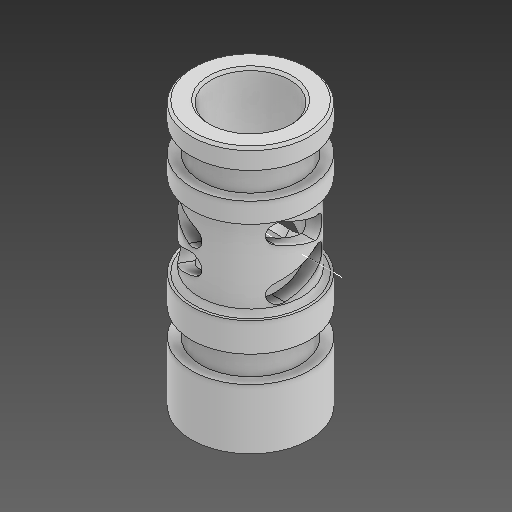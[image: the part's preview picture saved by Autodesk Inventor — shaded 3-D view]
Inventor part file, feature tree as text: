
AUTODESK INVENTOR PART (.ipt)
format: ipt  version: 2021 (Build 250183000, 183)  size: 296,448 bytes
history: native  units: in
note: dims shown in document units (in); Inventor stores cm internally (conversion verified against a paired STEP export)
features: other x7, sketch x5, plane x1
ambient origin geometry x8: Origin, YZ Plane, XZ Plane, XY Plane, X Axis, Y Axis, Z Axis, Center Point
bodies: Solid1 (feature_tree)
feature tree (13):
  other  "outer_sleeve.ipt"
  other  "Solid1::outer_sleeve.ipt"
  other  "TaggingFeature1"
  sketch  "Sketch2"  dims[d0=0.3937in]
  sketch  "Sketch3"
  sketch  "Sketch4"
  sketch  "Sketch5"
  sketch  "Sketch10"
  plane  "Work Plane1"
  other  "Work Axis1"
  other  "Work Axis2"
  other  "Srf1"
  other  "Srf1::Derived"
